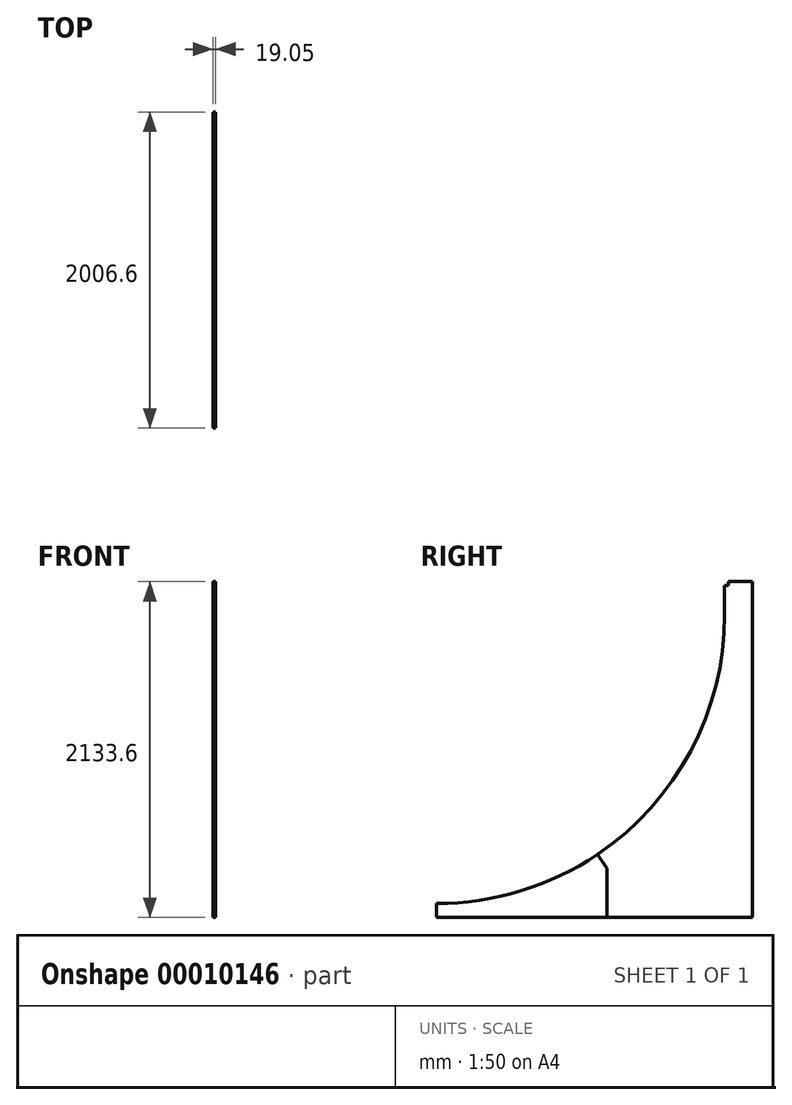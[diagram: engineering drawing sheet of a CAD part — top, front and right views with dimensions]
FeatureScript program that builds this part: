
annotation { "Feature Type Name" : "Feature", "Feature Type Description" : "" }
export const myFeature = defineFeature(function(context is Context, id is Id, definition is map)
    precondition{}
    {
        {
            var Q0;
            Q0=qCreatedBy(makeId("Right.planeOp"),FACE);
            var sketch = newSketch(context, id + "F0", { "sketchPlane" : qUnion([Q0])});
            skLineSegment(sketch, "E0", {"start": v(0, 0) * mm, "end": v(0, 88.9) * mm});
            skLineSegment(sketch, "E1", {"start": v(1828.8, 2133.6) * mm, "end": v(2006.6, 2133.6) * mm});
            skLineSegment(sketch, "E2", {"start": v(2006.6, 2133.6) * mm, "end": v(2006.6, 0) * mm});
            skLineSegment(sketch, "E3", {"start": v(2006.6, 0) * mm, "end": v(0, 0) * mm});
            skLineSegment(sketch, "E4", {"start": v(1828.8, 2133.6) * mm, "end": v(1828.8, 1917.7) * mm});
            skArc(sketch, "E5", {"start": v(0, 88.9) * mm, "mid": v(1293.16, 624.54) * mm, "end": v(1828.8, 1917.7) * mm});
            skLineSegment(sketch, "E6", {"start": v(1079.9, 312.65) * mm, "end": v(1020.88, 400.36) * mm});
            skLineSegment(sketch, "E7", {"start": v(1079.9, 312.65) * mm, "end": v(1079.9, 0) * mm});
            skSolve(sketch);
        }
        {
            var Q0;
            {var subQ3=sQuery(id+"F0.wireOp",EDGE,"E0");Q0=makeQuery(id+"F0.imprint","IMPRINT",FACE,{"disambiguationData":[TD([[makeQuery(id+"F0.imprint","IMPRINT",EDGE,{"derivedFrom":subQ3}),-1.0]])]});}
            extrude(context, id + "F1", {"entities" : qUnion([Q0]), "depth" : 19.05 * mm});
        }
        {
            var Q0;
            Q0=makeQuery(id+"F0.imprint","IMPRINT",FACE,{"disambiguationData":[TD([[makeQuery(id+"F0.imprint","IMPRINT",EDGE,{"derivedFrom":sQuery(id+"F0.wireOp",EDGE,"E1")}),-1.0]])]});
            extrude(context, id + "F2", {"entities" : qUnion([Q0]), "depth" : 19.05 * mm});
        }
        {
            var Q0;
            Q0=makeQuery(id+"F2.opExtrude","CAP_FACE",FACE,{"disambiguationData":[OSD([sQuery(id+"F0.wireOp",EDGE,"E1"),sQuery(id+"F0.wireOp",EDGE,"E2"),sQuery(id+"F0.wireOp",EDGE,"E3"),sQuery(id+"F0.wireOp",EDGE,"E4"),sQuery(id+"F0.wireOp",EDGE,"E5"),sQuery(id+"F0.wireOp",EDGE,"E6"),sQuery(id+"F0.wireOp",EDGE,"E7")])],"isStart":false});
            var sketch = newSketch(context, id + "F3", { "sketchPlane" : qUnion([Q0])});
            skLineSegment(sketch, "E8", {"start": v(1828.8, 2133.6) * mm, "end": v(1828.8, 2108.2) * mm});
            skLineSegment(sketch, "E9", {"start": v(1828.8, 2108.2) * mm, "end": v(1854.2, 2108.2) * mm});
            skLineSegment(sketch, "E10", {"start": v(1854.2, 2108.2) * mm, "end": v(1854.2, 2133.6) * mm});
            skLineSegment(sketch, "E11", {"start": v(1854.2, 2133.6) * mm, "end": v(1828.8, 2133.6) * mm});
            skSolve(sketch);
        }
        {
            var Q0;
            Q0 = qSketchRegion(id + "F3", true);
            extrude(context, id + "F4", {"entities" : qUnion([Q0]), "operationType" : NewBodyOperationType.REMOVE, "endBound" : BoundingType.THROUGH_ALL, "oppositeDirection" : true, "depth" : 25.4 * mm});
        }
    });
